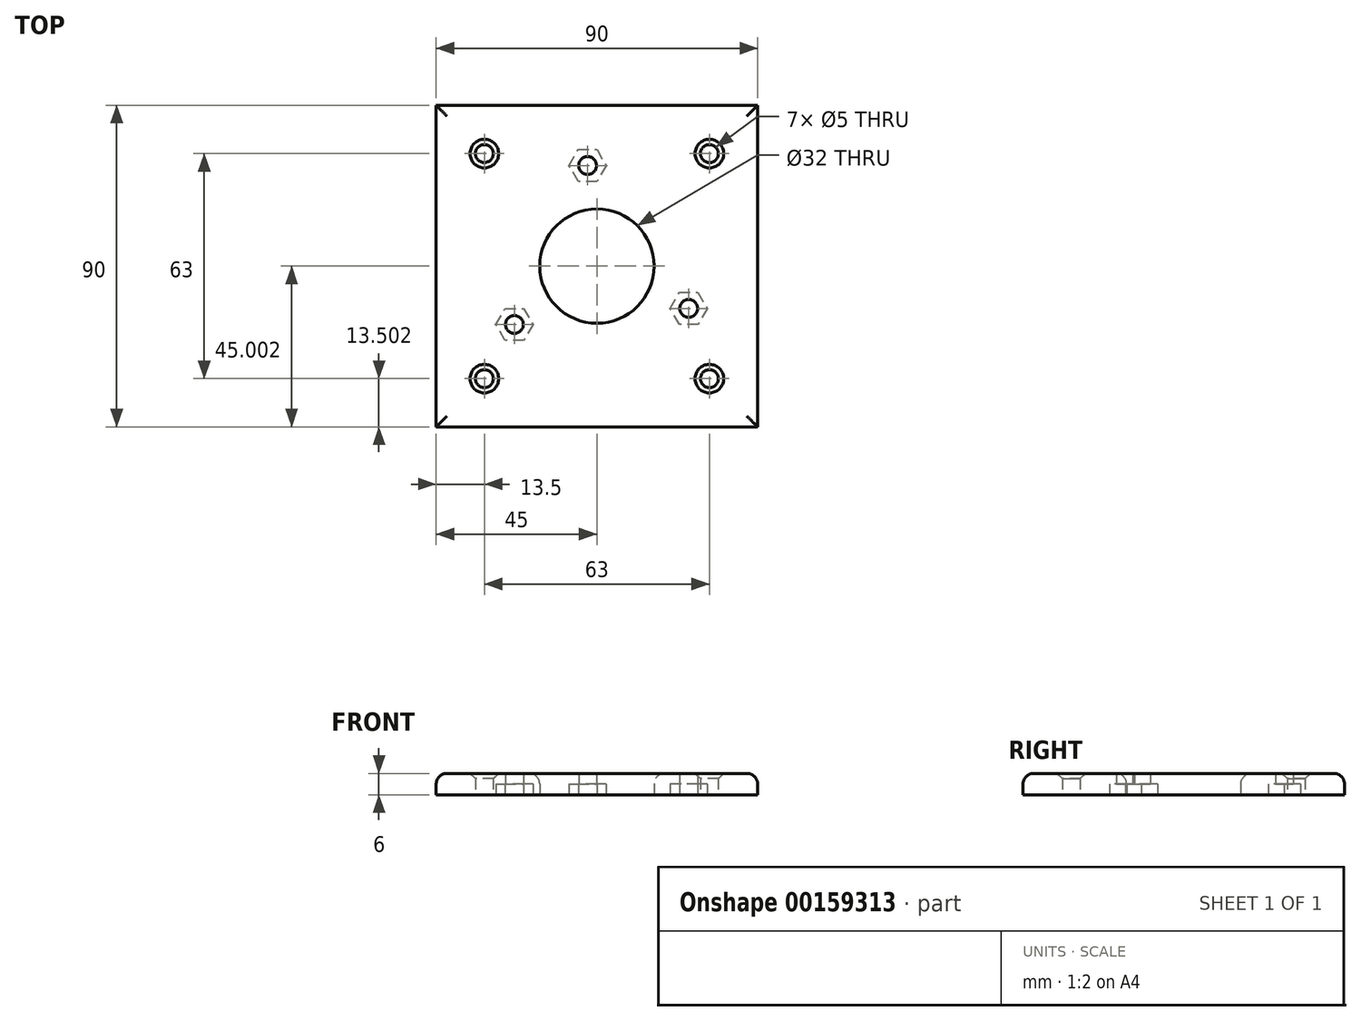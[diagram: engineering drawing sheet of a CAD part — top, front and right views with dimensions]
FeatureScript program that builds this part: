
annotation { "Feature Type Name" : "Feature", "Feature Type Description" : "" }
export const myFeature = defineFeature(function(context is Context, id is Id, definition is map)
    precondition{}
    {
        {
            var Q0;
            Q0=qCreatedBy(makeId("Top.planeOp"),FACE);
            var sketch = newSketch(context, id + "F0", { "sketchPlane" : qUnion([Q0])});
            skLineSegment(sketch, "E0.bottom", {"start": v(0, 12.96) * mm, "end": v(90, 12.96) * mm});
            skLineSegment(sketch, "E0.top", {"start": v(0, 102.96) * mm, "end": v(90, 102.96) * mm});
            skLineSegment(sketch, "E0.left", {"start": v(0, 12.96) * mm, "end": v(0, 102.96) * mm});
            skLineSegment(sketch, "E0.right", {"start": v(90, 12.96) * mm, "end": v(90, 102.96) * mm});
            skCircle(sketch, "E1", {"center": v(45, 57.96) * mm, "radius": 16 * mm});
            skCircle(sketch, "E2", {"center": v(21.9, 41.63) * mm, "radius": 2.5 * mm});
            skCircle(sketch, "E3", {"center": v(70.7, 46.13) * mm, "radius": 2.5 * mm});
            skCircle(sketch, "E4", {"center": v(42.4, 86.13) * mm, "radius": 2.5 * mm});
            skCircle(sketch, "E5", {"center": v(13.5, 89.46) * mm, "radius": 2.5 * mm});
            skCircle(sketch, "E6", {"center": v(76.5, 89.46) * mm, "radius": 2.5 * mm});
            skCircle(sketch, "E7", {"center": v(13.5, 26.46) * mm, "radius": 2.5 * mm});
            skCircle(sketch, "E8", {"center": v(76.5, 26.46) * mm, "radius": 2.5 * mm});
            skCircle(sketch, "E9.cCircle", {"center": v(21.9, 41.63) * mm, "radius": 4.5 * mm, "construction": true});
            skLineSegment(sketch, "E9.0", {"start": v(27.1, 41.63) * mm, "end": v(24.5, 37.13) * mm});
            skLineSegment(sketch, "E9.1", {"start": v(24.5, 37.13) * mm, "end": v(19.3, 37.13) * mm});
            skLineSegment(sketch, "E9.2", {"start": v(19.3, 37.13) * mm, "end": v(16.7, 41.63) * mm});
            skLineSegment(sketch, "E9.3", {"start": v(16.7, 41.63) * mm, "end": v(19.3, 46.13) * mm});
            skLineSegment(sketch, "E9.4", {"start": v(19.3, 46.13) * mm, "end": v(24.5, 46.13) * mm});
            skLineSegment(sketch, "E9.5", {"start": v(24.5, 46.13) * mm, "end": v(27.1, 41.63) * mm});
            skPoint(sketch, "E9.0.midPoint", {"position": v(25.8, 39.38) * mm});
            skCircle(sketch, "E10.cCircle", {"center": v(70.7, 46.13) * mm, "radius": 4.5 * mm, "construction": true});
            skLineSegment(sketch, "E10.0", {"start": v(73.3, 41.63) * mm, "end": v(68.1, 41.63) * mm});
            skLineSegment(sketch, "E10.1", {"start": v(68.1, 41.63) * mm, "end": v(65.5, 46.13) * mm});
            skLineSegment(sketch, "E10.2", {"start": v(65.5, 46.13) * mm, "end": v(68.1, 50.63) * mm});
            skLineSegment(sketch, "E10.3", {"start": v(68.1, 50.63) * mm, "end": v(73.3, 50.63) * mm});
            skLineSegment(sketch, "E10.4", {"start": v(73.3, 50.63) * mm, "end": v(75.9, 46.13) * mm});
            skLineSegment(sketch, "E10.5", {"start": v(75.9, 46.13) * mm, "end": v(73.3, 41.63) * mm});
            skPoint(sketch, "E10.0.midPoint", {"position": v(70.7, 41.63) * mm});
            skCircle(sketch, "E11.cCircle", {"center": v(42.4, 86.13) * mm, "radius": 4.5 * mm, "construction": true});
            skLineSegment(sketch, "E11.0", {"start": v(39.8, 81.63) * mm, "end": v(37.2, 86.13) * mm});
            skLineSegment(sketch, "E11.1", {"start": v(37.2, 86.13) * mm, "end": v(39.8, 90.63) * mm});
            skLineSegment(sketch, "E11.2", {"start": v(39.8, 90.63) * mm, "end": v(45, 90.63) * mm});
            skLineSegment(sketch, "E11.3", {"start": v(45, 90.63) * mm, "end": v(47.6, 86.13) * mm});
            skLineSegment(sketch, "E11.4", {"start": v(47.6, 86.13) * mm, "end": v(45, 81.63) * mm});
            skLineSegment(sketch, "E11.5", {"start": v(45, 81.63) * mm, "end": v(39.8, 81.63) * mm});
            skPoint(sketch, "E11.0.midPoint", {"position": v(38.5, 83.88) * mm});
            skLineSegment(sketch, "E12", {"start": v(0, 102.96) * mm, "end": v(13.5, 89.46) * mm});
            skLineSegment(sketch, "E13", {"start": v(0, 12.96) * mm, "end": v(13.5, 26.46) * mm});
            skCircle(sketch, "E14.cCircle", {"center": v(45, 57.96) * mm, "radius": 28.3 * mm, "construction": true});
            skLineSegment(sketch, "E14.0", {"start": v(42.4, 86.13) * mm, "end": v(70.7, 46.13) * mm});
            skLineSegment(sketch, "E14.1", {"start": v(70.7, 46.13) * mm, "end": v(21.9, 41.63) * mm});
            skLineSegment(sketch, "E14.2", {"start": v(21.9, 41.63) * mm, "end": v(42.4, 86.13) * mm});
            skLineSegment(sketch, "E15.trimOffspring", {"start": v(33.69, 69.28) * mm, "end": v(56.31, 46.65) * mm});
            skLineSegment(sketch, "E16.trimOffspring", {"start": v(76.5, 89.46) * mm, "end": v(90, 102.96) * mm});
            skLineSegment(sketch, "E17.trimOffspring", {"start": v(24.96, 37.92) * mm, "end": v(25, 37.96) * mm});
            skLineSegment(sketch, "E18.trimOffspring", {"start": v(76.5, 26.46) * mm, "end": v(90, 12.96) * mm});
            skLineSegment(sketch, "E19.trimOffspring", {"start": v(33.69, 46.65) * mm, "end": v(56.31, 69.28) * mm});
            skSolve(sketch);
        }
        {
            var Q0;
            {var subQ0=sQuery(id+"F0.wireOp",EDGE,"E11.0");Q0=makeQuery(id+"F0.imprint","IMPRINT",FACE,{"disambiguationData":[TD([[makeQuery(id+"F0.imprint","IMPRINT",EDGE,{"derivedFrom":subQ0}),-1.0]])]});}
            var Q1;
            {var subQ0=sQuery(id+"F0.wireOp",EDGE,"E14.0");var subQ1=sQuery(id+"F0.wireOp",EDGE,"E4");var subQ2=makeQuery(id+"F0.imprint","INTERSECT",VERTEX,{"derivedFrom":[subQ1,subQ0]});Q1=makeQuery(id+"F0.imprint","IMPRINT",FACE,{"disambiguationData":[TD([[makeQuery(id+"F0.imprint","IMPRINT",EDGE,{"disambiguationData":[TD([[subQ2,1.0]])],"derivedFrom":subQ1}),-1.0]])]});}
            var Q2;
            Q2=makeQuery(id+"F0.imprint","IMPRINT",FACE,{"disambiguationData":[TD([[makeQuery(id+"F0.imprint","IMPRINT",EDGE,{"derivedFrom":sQuery(id+"F0.wireOp",EDGE,"E0.bottom")}),1.0]])]});
            var Q3;
            {var subQ0=sQuery(id+"F0.wireOp",EDGE,"E9.1");Q3=makeQuery(id+"F0.imprint","IMPRINT",FACE,{"disambiguationData":[TD([[makeQuery(id+"F0.imprint","IMPRINT",EDGE,{"derivedFrom":subQ0}),-1.0]])]});}
            var Q4;
            {var subQ0=sQuery(id+"F0.wireOp",EDGE,"E14.1");var subQ1=sQuery(id+"F0.wireOp",EDGE,"E2");var subQ2=makeQuery(id+"F0.imprint","INTERSECT",VERTEX,{"derivedFrom":[subQ1,subQ0]});Q4=makeQuery(id+"F0.imprint","IMPRINT",FACE,{"disambiguationData":[TD([[makeQuery(id+"F0.imprint","IMPRINT",EDGE,{"disambiguationData":[TD([[subQ2,-1.0]])],"derivedFrom":subQ1}),-1.0]])]});}
            var Q5;
            {var subQ7=sQuery(id+"F0.wireOp",EDGE,"E1");var subQ8=makeQuery(id+"F0.imprint","INTERSECT",VERTEX,{"disambiguationData":[OD(0.0)],"derivedFrom":[subQ7,sQuery(id+"F0.wireOp",EDGE,"E19.trimOffspring")]});Q5=makeQuery(id+"F0.imprint","IMPRINT",FACE,{"disambiguationData":[TD([[makeQuery(id+"F0.imprint","IMPRINT",EDGE,{"disambiguationData":[TD([[subQ8,1.0]])],"derivedFrom":subQ7}),-1.0]])]});}
            var Q6;
            {var subQ5=sQuery(id+"F0.wireOp",EDGE,"E14.0");var subQ7=sQuery(id+"F0.wireOp",EDGE,"E1");var subQ8=makeQuery(id+"F0.imprint","INTERSECT",VERTEX,{"disambiguationData":[OD(1.0)],"derivedFrom":[subQ7,subQ5]});Q6=makeQuery(id+"F0.imprint","IMPRINT",FACE,{"disambiguationData":[TD([[makeQuery(id+"F0.imprint","IMPRINT",EDGE,{"disambiguationData":[TD([[subQ8,-1.0]])],"derivedFrom":subQ7}),-1.0]])]});}
            var Q7;
            {var subQ5=sQuery(id+"F0.wireOp",EDGE,"E1");var subQ6=makeQuery(id+"F0.imprint","INTERSECT",VERTEX,{"disambiguationData":[OD(1.0)],"derivedFrom":[subQ5,sQuery(id+"F0.wireOp",EDGE,"E15.trimOffspring")]});Q7=makeQuery(id+"F0.imprint","IMPRINT",FACE,{"disambiguationData":[TD([[makeQuery(id+"F0.imprint","IMPRINT",EDGE,{"disambiguationData":[TD([[subQ6,1.0]])],"derivedFrom":subQ5}),-1.0]])]});}
            var Q8;
            {var subQ3=sQuery(id+"F0.wireOp",EDGE,"E14.0");var subQ5=sQuery(id+"F0.wireOp",EDGE,"E3");var subQ6=makeQuery(id+"F0.imprint","INTERSECT",VERTEX,{"derivedFrom":[subQ5,subQ3]});Q8=makeQuery(id+"F0.imprint","IMPRINT",FACE,{"disambiguationData":[TD([[makeQuery(id+"F0.imprint","IMPRINT",EDGE,{"disambiguationData":[TD([[subQ6,-1.0]])],"derivedFrom":subQ5}),-1.0]])]});}
            var Q9;
            {var subQ9=sQuery(id+"F0.wireOp",EDGE,"E10.0");Q9=makeQuery(id+"F0.imprint","IMPRINT",FACE,{"disambiguationData":[TD([[makeQuery(id+"F0.imprint","IMPRINT",EDGE,{"derivedFrom":subQ9}),-1.0]])]});}
            extrude(context, id + "F1", {"entities" : qUnion([Q0, Q1, Q2, Q3, Q4, Q5, Q6, Q7, Q8, Q9]), "depth" : 6 * mm});
        }
        {
            var Q0;
            Q0=makeQuery(id+"F0.imprint","IMPRINT",FACE,{"disambiguationData":[TD([[makeQuery(id+"F0.imprint","IMPRINT",EDGE,{"derivedFrom":sQuery(id+"F0.wireOp",EDGE,"E4")}),-1.0]])]});
            var Q1;
            Q1=makeQuery(id+"F0.imprint","IMPRINT",FACE,{"disambiguationData":[TD([[makeQuery(id+"F0.imprint","IMPRINT",EDGE,{"derivedFrom":sQuery(id+"F0.wireOp",EDGE,"E2")}),-1.0]])]});
            var Q2;
            Q2=makeQuery(id+"F0.imprint","IMPRINT",FACE,{"disambiguationData":[TD([[makeQuery(id+"F0.imprint","IMPRINT",EDGE,{"derivedFrom":sQuery(id+"F0.wireOp",EDGE,"E3")}),-1.0]])]});
            var Q3;
            {var subQ0=sQuery(id+"F0.wireOp",EDGE,"E9.1");Q3=makeQuery(id+"F0.imprint","IMPRINT",FACE,{"disambiguationData":[TD([[makeQuery(id+"F0.imprint","IMPRINT",EDGE,{"derivedFrom":subQ0}),-1.0]])]});}
            var Q4;
            {var subQ9=sQuery(id+"F0.wireOp",EDGE,"E10.0");Q4=makeQuery(id+"F0.imprint","IMPRINT",FACE,{"disambiguationData":[TD([[makeQuery(id+"F0.imprint","IMPRINT",EDGE,{"derivedFrom":subQ9}),-1.0]])]});}
            var Q5;
            {var subQ0=sQuery(id+"F0.wireOp",EDGE,"E11.0");Q5=makeQuery(id+"F0.imprint","IMPRINT",FACE,{"disambiguationData":[TD([[makeQuery(id+"F0.imprint","IMPRINT",EDGE,{"derivedFrom":subQ0}),-1.0]])]});}
            extrude(context, id + "F2", {"entities" : qUnion([Q0, Q1, Q2, Q3, Q4, Q5]), "operationType" : NewBodyOperationType.REMOVE, "depth" : 3 * mm});
        }
        {
            var Q0;
            Q0=makeQuery(id+"F1.opExtrude","CAP_EDGE",EDGE,{"disambiguationData":[OSD([sQuery(id+"F0.wireOp",EDGE,"E0.left")])],"isStart":false});
            var Q1;
            Q1=makeQuery(id+"F1.opExtrude","CAP_EDGE",EDGE,{"disambiguationData":[OSD([sQuery(id+"F0.wireOp",EDGE,"E0.bottom")])],"isStart":false});
            var Q2;
            Q2=makeQuery(id+"F1.opExtrude","CAP_EDGE",EDGE,{"disambiguationData":[OSD([sQuery(id+"F0.wireOp",EDGE,"E0.top")])],"isStart":false});
            var Q3;
            Q3=makeQuery(id+"F1.opExtrude","CAP_EDGE",EDGE,{"disambiguationData":[OSD([sQuery(id+"F0.wireOp",EDGE,"E0.right")])],"isStart":false});
            var Q4;
            Q4=makeQuery(id+"F1.opExtrude","CAP_EDGE",EDGE,{"disambiguationData":[OSD([sQuery(id+"F0.wireOp",EDGE,"E1")])],"isStart":false});
            fillet(context, id + "F3", {"entities" : qUnion([Q0, Q1, Q2, Q3, Q4]), "radius" : 3 * mm, "tangentPropagation" : true, "allowEdgeOverflow" : false});
        }
        {
            var Q0;
            Q0=makeQuery(id+"F1.opExtrude","CAP_EDGE",EDGE,{"disambiguationData":[OSD([sQuery(id+"F0.wireOp",EDGE,"E5")])],"isStart":false});
            var Q1;
            Q1=makeQuery(id+"F1.opExtrude","CAP_EDGE",EDGE,{"disambiguationData":[OSD([sQuery(id+"F0.wireOp",EDGE,"E6")])],"isStart":false});
            var Q2;
            Q2=makeQuery(id+"F1.opExtrude","CAP_EDGE",EDGE,{"disambiguationData":[OSD([sQuery(id+"F0.wireOp",EDGE,"E8")])],"isStart":false});
            var Q3;
            Q3=makeQuery(id+"F1.opExtrude","CAP_EDGE",EDGE,{"disambiguationData":[OSD([sQuery(id+"F0.wireOp",EDGE,"E7")])],"isStart":false});
            chamfer(context, id + "F4", {"entities" : qUnion([Q0, Q1, Q2, Q3]), "width" : 1.5 * mm, "tangentPropagation" : true});
        }
    });
